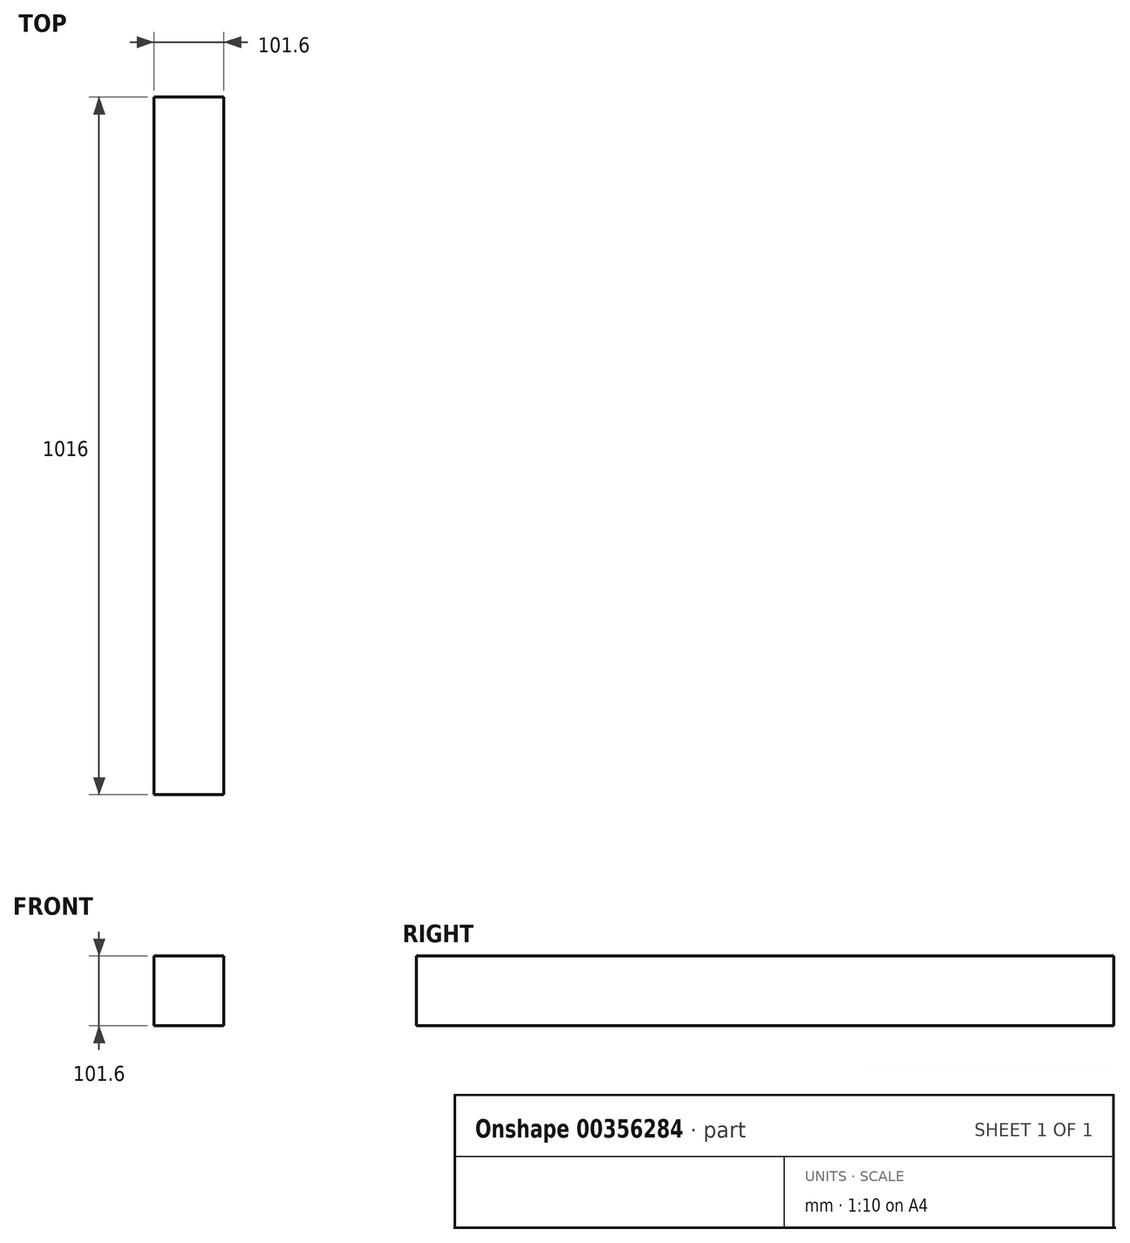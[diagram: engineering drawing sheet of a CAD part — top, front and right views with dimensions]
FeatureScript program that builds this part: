
annotation { "Feature Type Name" : "Feature", "Feature Type Description" : "" }
export const myFeature = defineFeature(function(context is Context, id is Id, definition is map)
    precondition{}
    {
        {
            var Q0;
            Q0=qCreatedBy(makeId("Right.planeOp"),FACE);
            var sketch = newSketch(context, id + "F0", { "sketchPlane" : qUnion([Q0])});
            skLineSegment(sketch, "E0.bottom", {"start": v(-370.68, 79.04) * mm, "end": v(645.32, 79.04) * mm});
            skLineSegment(sketch, "E0.top", {"start": v(-370.68, -22.56) * mm, "end": v(645.32, -22.56) * mm});
            skLineSegment(sketch, "E0.left", {"start": v(-370.68, 79.04) * mm, "end": v(-370.68, -22.56) * mm});
            skLineSegment(sketch, "E0.right", {"start": v(645.32, 79.04) * mm, "end": v(645.32, -22.56) * mm});
            skSolve(sketch);
        }
        {
            var Q0;
            Q0 = qSketchRegion(id + "F0", true);
            extrude(context, id + "F1", {"entities" : qUnion([Q0]), "depth" : 101.6 * mm});
        }
    });
